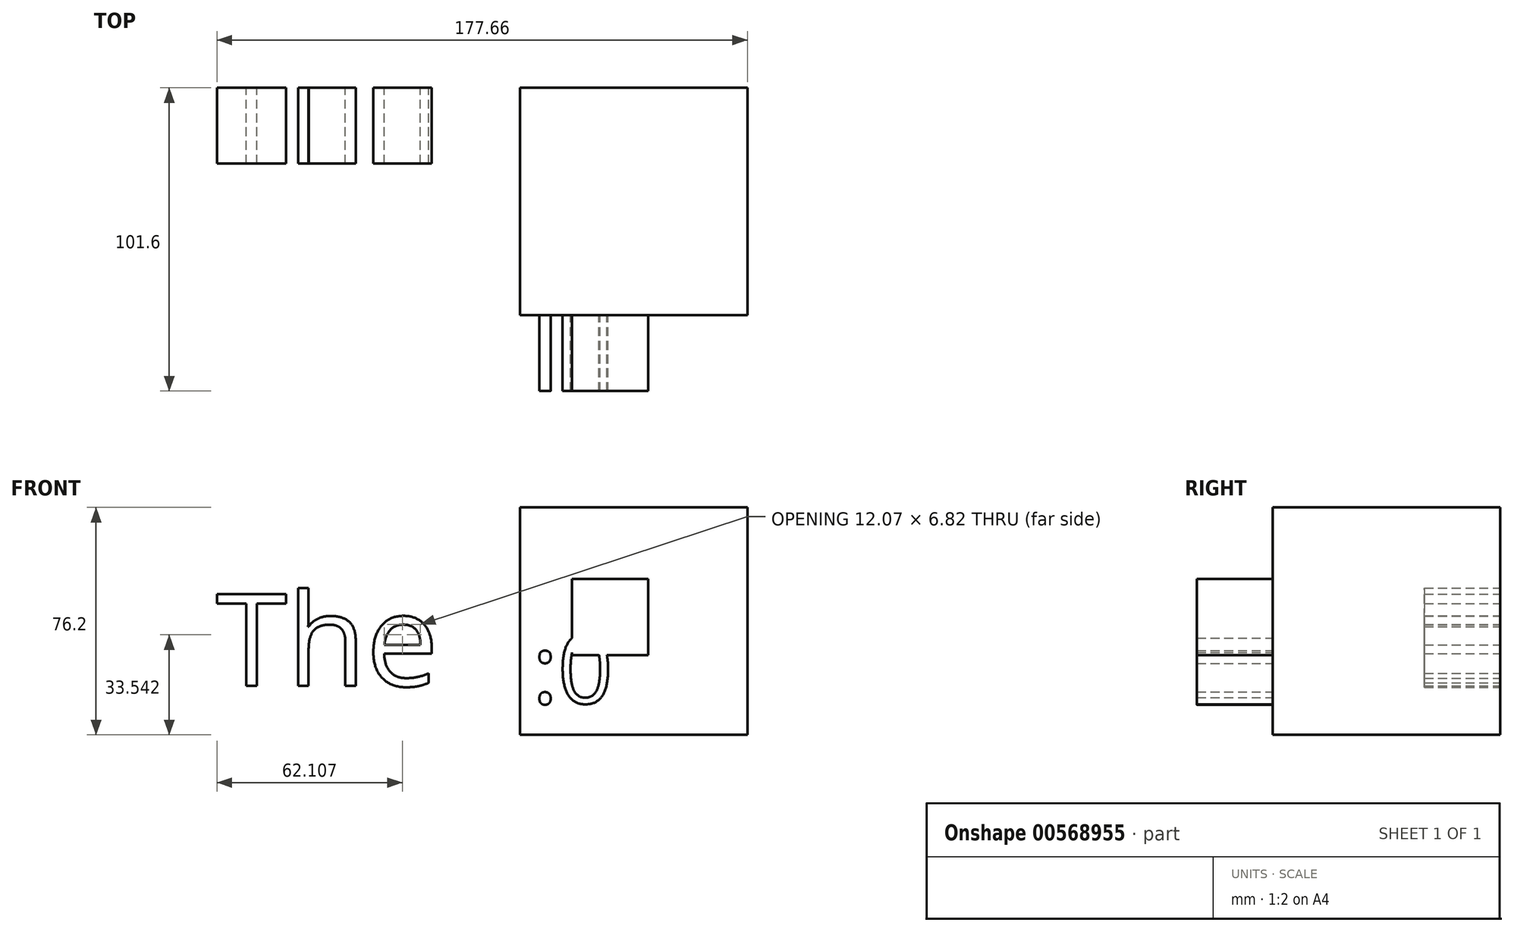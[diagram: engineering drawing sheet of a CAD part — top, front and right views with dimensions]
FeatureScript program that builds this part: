
annotation { "Feature Type Name" : "Feature", "Feature Type Description" : "" }
export const myFeature = defineFeature(function(context is Context, id is Id, definition is map)
    precondition{}
    {
        {
            var Q0;
            Q0=qCreatedBy(makeId("Front.planeOp"),FACE);
            var sketch = newSketch(context, id + "F0", { "sketchPlane" : qUnion([Q0])});
            skLineSegment(sketch, "E0.bottom", {"start": v(0, 0) * mm, "end": v(76.2, 0) * mm});
            skLineSegment(sketch, "E0.top", {"start": v(0, 76.2) * mm, "end": v(76.2, 76.2) * mm});
            skLineSegment(sketch, "E0.left", {"start": v(0, 0) * mm, "end": v(0, 76.2) * mm});
            skLineSegment(sketch, "E0.right", {"start": v(76.2, 0) * mm, "end": v(76.2, 76.2) * mm});
            skSolve(sketch);
        }
        {
            var Q0;
            Q0=makeQuery(id+"F0.imprint","IMPRINT",FACE,{"disambiguationData":[TD([[makeQuery(id+"F0.imprint","IMPRINT",EDGE,{"derivedFrom":sQuery(id+"F0.wireOp",EDGE,"E0.bottom")}),1.0]])]});
            extrude(context, id + "F1", {"entities" : qUnion([Q0]), "depth" : 76.2 * mm, "offsetDistance" : 25.4 * mm});
        }
        {
            var Q0;
            Q0=makeQuery(id+"F1.opExtrude","CAP_FACE",FACE,{"disambiguationData":[OSD([sQuery(id+"F0.wireOp",EDGE,"E0.bottom"),sQuery(id+"F0.wireOp",EDGE,"E0.top"),sQuery(id+"F0.wireOp",EDGE,"E0.left"),sQuery(id+"F0.wireOp",EDGE,"E0.right")])],"isStart":false});
            var sketch = newSketch(context, id + "F2", { "sketchPlane" : qUnion([Q0])});
            skLineSegment(sketch, "E1.bottom", {"start": v(42.97, 26.78) * mm, "end": v(17.49, 26.78) * mm});
            skLineSegment(sketch, "E1.top", {"start": v(42.97, 52.26) * mm, "end": v(17.49, 52.26) * mm});
            skLineSegment(sketch, "E1.left", {"start": v(42.97, 26.78) * mm, "end": v(42.97, 52.26) * mm});
            skLineSegment(sketch, "E1.right", {"start": v(17.49, 26.78) * mm, "end": v(17.49, 52.26) * mm});
            skSolve(sketch);
        }
        {
            var Q0;
            Q0=makeQuery(id+"F2.imprint","IMPRINT",FACE,{"disambiguationData":[TD([[makeQuery(id+"F2.imprint","IMPRINT",EDGE,{"derivedFrom":sQuery(id+"F2.wireOp",EDGE,"E1.bottom")}),-1.0]])]});
            extrude(context, id + "F3", {"entities" : qUnion([Q0]), "operationType" : NewBodyOperationType.ADD, "depth" : 25.4 * mm, "offsetDistance" : 25.4 * mm});
        }
        {
            var Q0;
            Q0=makeQuery(id+"F1.opExtrude","CAP_FACE",FACE,{"disambiguationData":[OSD([sQuery(id+"F0.wireOp",EDGE,"E0.bottom"),sQuery(id+"F0.wireOp",EDGE,"E0.top"),sQuery(id+"F0.wireOp",EDGE,"E0.left"),sQuery(id+"F0.wireOp",EDGE,"E0.right")])],"isStart":false});
            var sketch = newSketch(context, id + "F4", { "sketchPlane" : qUnion([Q0])});
            skSolve(sketch);
        }
        {
            var Q0;
            Q0=makeQuery(id+"F4.imprint","IMPRINT",FACE,{"disambiguationData":[TD([[makeQuery(id+"F4.imprint","IMPRINT",EDGE,{"derivedFrom":makeQuery(id+"F1.opExtrude","CAP_EDGE",EDGE,{"disambiguationData":[OSD([sQuery(id+"F0.wireOp",EDGE,"E0.bottom")])],"isStart":false})}),1.0]])]});
            var sketch = newSketch(context, id + "F5", { "sketchPlane" : qUnion([Q0])});
            skText(sketch, "E2", { "text": ":0", "fontName": "OpenSans-Regular.ttf"});
            const initialGuessF5  = {"E2": [0.00414, 0.01054, 1, 0, 0.0232]};
            skSetInitialGuess(sketch, initialGuessF5);
            skSolve(sketch);
        }
        {
            var Q0;
            Q0 = qSketchRegion(id + "F5", true);
            extrude(context, id + "F6", {"entities" : qUnion([Q0]), "operationType" : NewBodyOperationType.ADD, "depth" : 25.4 * mm, "offsetDistance" : 25.4 * mm});
        }
        {
            var Q0;
            Q0=qCreatedBy(makeId("Front.planeOp"),FACE);
            var sketch = newSketch(context, id + "F7", { "sketchPlane" : qUnion([Q0])});
            skText(sketch, "E3", { "text": "The", "fontName": "OpenSans-Regular.ttf"});
            const initialGuessF7  = {"E3": [-0.10184, 0.01638, 1, 0, 0.03105]};
            skSetInitialGuess(sketch, initialGuessF7);
            skSolve(sketch);
        }
        {
            var Q0;
            Q0 = qSketchRegion(id + "F7", true);
            extrude(context, id + "F8", {"entities" : qUnion([Q0]), "depth" : 25.4 * mm, "offsetDistance" : 25.4 * mm});
        }
    });
